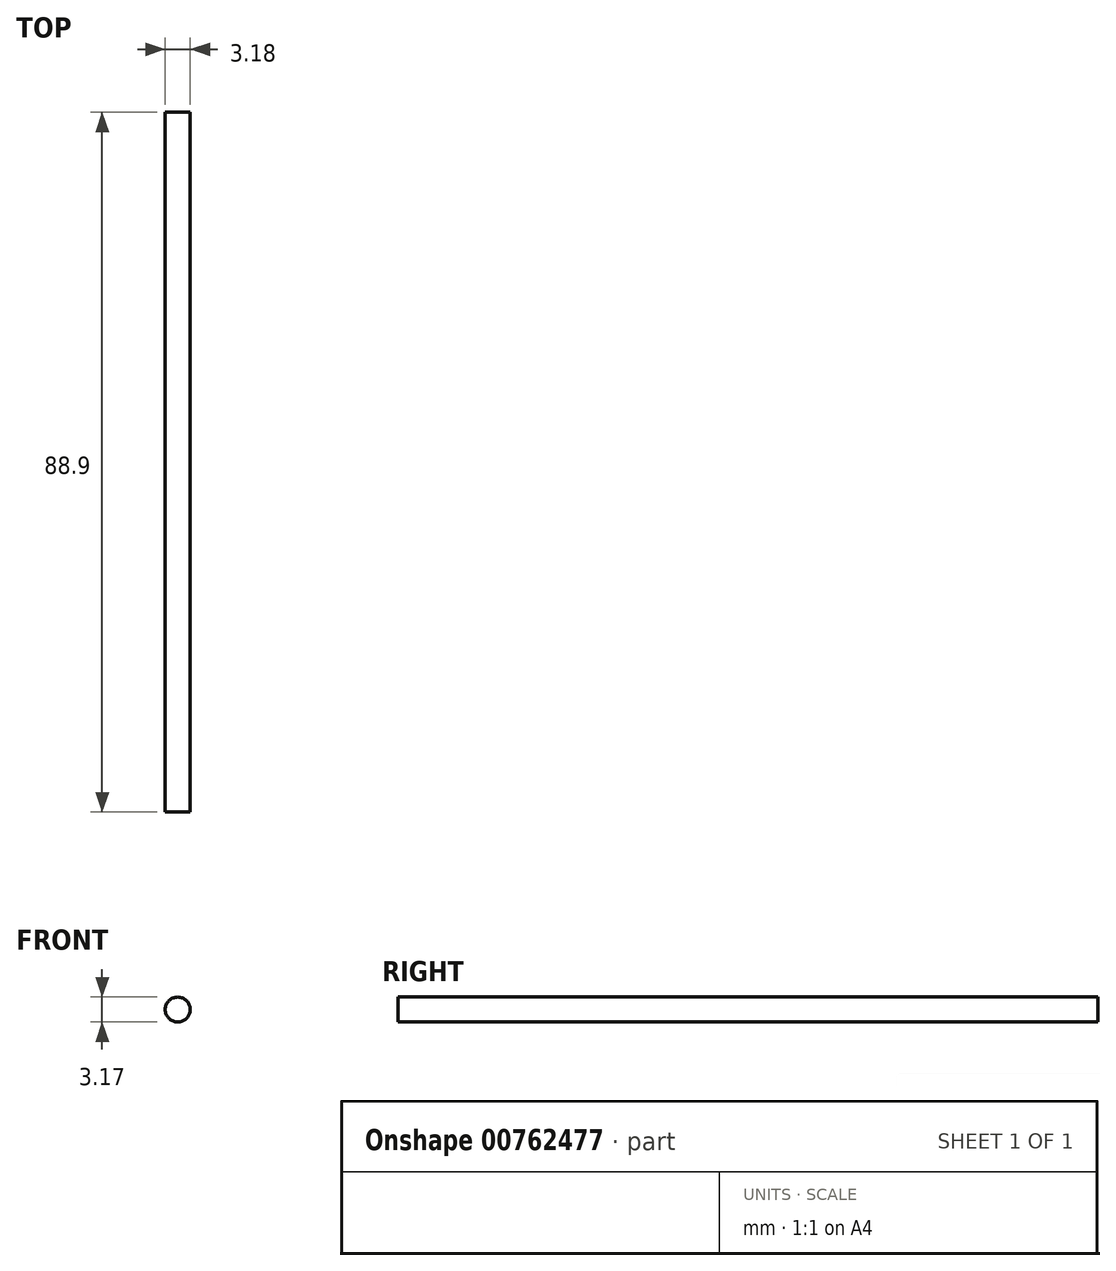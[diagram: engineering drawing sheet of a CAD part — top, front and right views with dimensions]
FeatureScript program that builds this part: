
annotation { "Feature Type Name" : "Feature", "Feature Type Description" : "" }
export const myFeature = defineFeature(function(context is Context, id is Id, definition is map)
    precondition{}
    {
        {
            var Q0;
            Q0=qCreatedBy(makeId("Front.planeOp"),FACE);
            var sketch = newSketch(context, id + "F0", { "sketchPlane" : qUnion([Q0])});
            skCircle(sketch, "E0", {"center": v(-43.85, 8.06) * mm, "radius": 1.59 * mm});
            skSolve(sketch);
        }
        {
            var Q0;
            Q0=makeQuery(id+"F0.imprint","IMPRINT",FACE,{"disambiguationData":[TD([[makeQuery(id+"F0.imprint","IMPRINT",EDGE,{"derivedFrom":sQuery(id+"F0.wireOp",EDGE,"E0")}),1.0]])]});
            extrude(context, id + "F1", {"entities" : qUnion([Q0]), "depth" : 88.9 * mm, "offsetDistance" : 25.4 * mm});
        }
    });
